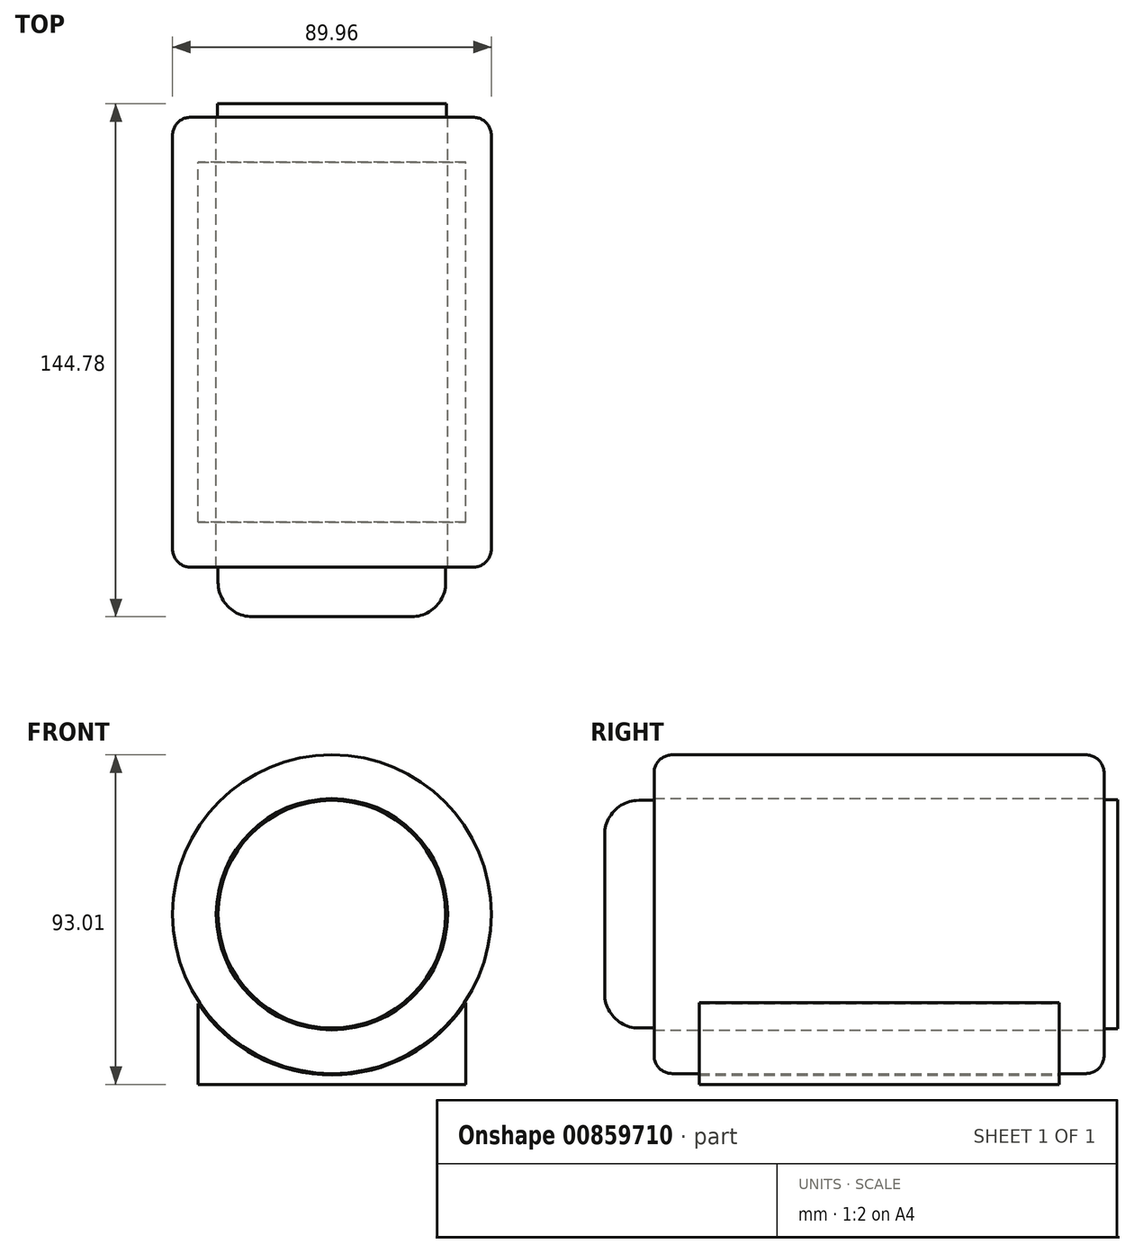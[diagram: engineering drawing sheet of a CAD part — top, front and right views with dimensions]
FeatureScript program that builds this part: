
annotation { "Feature Type Name" : "Feature", "Feature Type Description" : "" }
export const myFeature = defineFeature(function(context is Context, id is Id, definition is map)
    precondition{}
    {
        {
            var Q0;
            Q0=qCreatedBy(makeId("Front.planeOp"),FACE);
            var sketch = newSketch(context, id + "F0", { "sketchPlane" : qUnion([Q0])});
            skCircle(sketch, "E0", {"center": v(0, 0) * mm, "radius": 44.98 * mm});
            skCircle(sketch, "E1", {"center": v(0, 0) * mm, "radius": 32.66 * mm});
            skCircle(sketch, "E2", {"center": v(0, 0) * mm, "radius": 6.92 * mm});
            skSolve(sketch);
        }
        {
            var Q0;
            Q0=makeQuery(id+"F0.imprint","IMPRINT",FACE,{"disambiguationData":[TD([[makeQuery(id+"F0.imprint","IMPRINT",EDGE,{"derivedFrom":sQuery(id+"F0.wireOp",EDGE,"E0")}),1.0]])]});
            extrude(context, id + "F1", {"entities" : qUnion([Q0]), "endBound" : BoundingType.SYMMETRIC, "depth" : 127 * mm, "offsetDistance" : 25.4 * mm});
        }
        {
            var Q0;
            Q0=makeQuery(id+"F1.opExtrude","CAP_FACE",FACE,{"disambiguationData":[OSD([sQuery(id+"F0.wireOp",EDGE,"E0"),sQuery(id+"F0.wireOp",EDGE,"E1")])],"isStart":false});
            var sketch = newSketch(context, id + "F2", { "sketchPlane" : qUnion([Q0])});
            skCircle(sketch, "E3", {"center": v(0, 0) * mm, "radius": 32.13 * mm});
            skSolve(sketch);
        }
        {
            var Q0;
            Q0=qSketchRegion(id+"F2",true);
            extrude(context, id + "F3", {"entities" : qUnion([Q0]), "depth" : 13.97 * mm, "offsetDistance" : 25.4 * mm});
        }
        {
            var Q0;
            Q0=makeQuery(id+"F3.opExtrude","CAP_EDGE",EDGE,{"disambiguationData":[OSD([sQuery(id+"F2.wireOp",EDGE,"E3")])],"isStart":false});
            fillet(context, id + "F4", {"entities" : qUnion([Q0]), "radius" : 9.65 * mm, "tangentPropagation" : true, "allowEdgeOverflow" : false});
        }
        {
            var Q0;
            Q0=makeQuery(id+"F1.opExtrude","CAP_EDGE",EDGE,{"disambiguationData":[OSD([sQuery(id+"F0.wireOp",EDGE,"E0")])],"isStart":true});
            fillet(context, id + "F5", {"entities" : qUnion([Q0]), "radius" : 5.08 * mm, "tangentPropagation" : true, "allowEdgeOverflow" : false});
        }
        {
            var Q0;
            Q0=makeQuery(id+"F1.opExtrude","CAP_FACE",FACE,{"disambiguationData":[OSD([sQuery(id+"F0.wireOp",EDGE,"E0"),sQuery(id+"F0.wireOp",EDGE,"E1")])],"isStart":true});
            var sketch = newSketch(context, id + "F6", { "sketchPlane" : qUnion([Q0])});
            skCircle(sketch, "E4", {"center": v(0, 0) * mm, "radius": 32.29 * mm});
            skSolve(sketch);
        }
        {
            var Q0;
            Q0=qSketchRegion(id+"F6",true);
            extrude(context, id + "F7", {"entities" : qUnion([Q0]), "depth" : 3.8 * mm, "offsetDistance" : 25.4 * mm});
        }
        {
            var Q0;
            Q0=makeQuery(id+"F1.opExtrude","CAP_EDGE",EDGE,{"disambiguationData":[OSD([sQuery(id+"F0.wireOp",EDGE,"E0")])],"isStart":false});
            fillet(context, id + "F8", {"entities" : qUnion([Q0]), "radius" : 5.08 * mm, "tangentPropagation" : true, "allowEdgeOverflow" : false});
        }
        {
            var Q0;
            Q0=qCreatedBy(makeId("Front.planeOp"),FACE);
            var sketch = newSketch(context, id + "F9", { "sketchPlane" : qUnion([Q0])});
            skArc(sketch, "E5", {"start": v(-37.8, -25.24) * mm, "mid": v(0.06, -45.4) * mm, "end": v(37.8, -25) * mm});
            skLineSegment(sketch, "E6", {"start": v(37.8, -25) * mm, "end": v(37.8, -48.03) * mm});
            skLineSegment(sketch, "E7", {"start": v(37.8, -48.03) * mm, "end": v(-37.8, -48.03) * mm});
            skLineSegment(sketch, "E8", {"start": v(-37.8, -48.03) * mm, "end": v(-37.8, -25.24) * mm});
            skSolve(sketch);
        }
        {
            var Q0;
            Q0=makeQuery(id+"F9.imprint","IMPRINT",FACE,{"disambiguationData":[TD([[makeQuery(id+"F9.imprint","IMPRINT",EDGE,{"derivedFrom":sQuery(id+"F9.wireOp",EDGE,"E5")}),-1.0]])]});
            extrude(context, id + "F10", {"entities" : qUnion([Q0]), "endBound" : BoundingType.SYMMETRIC, "depth" : 101.6 * mm, "offsetDistance" : 25.4 * mm});
        }
    });
